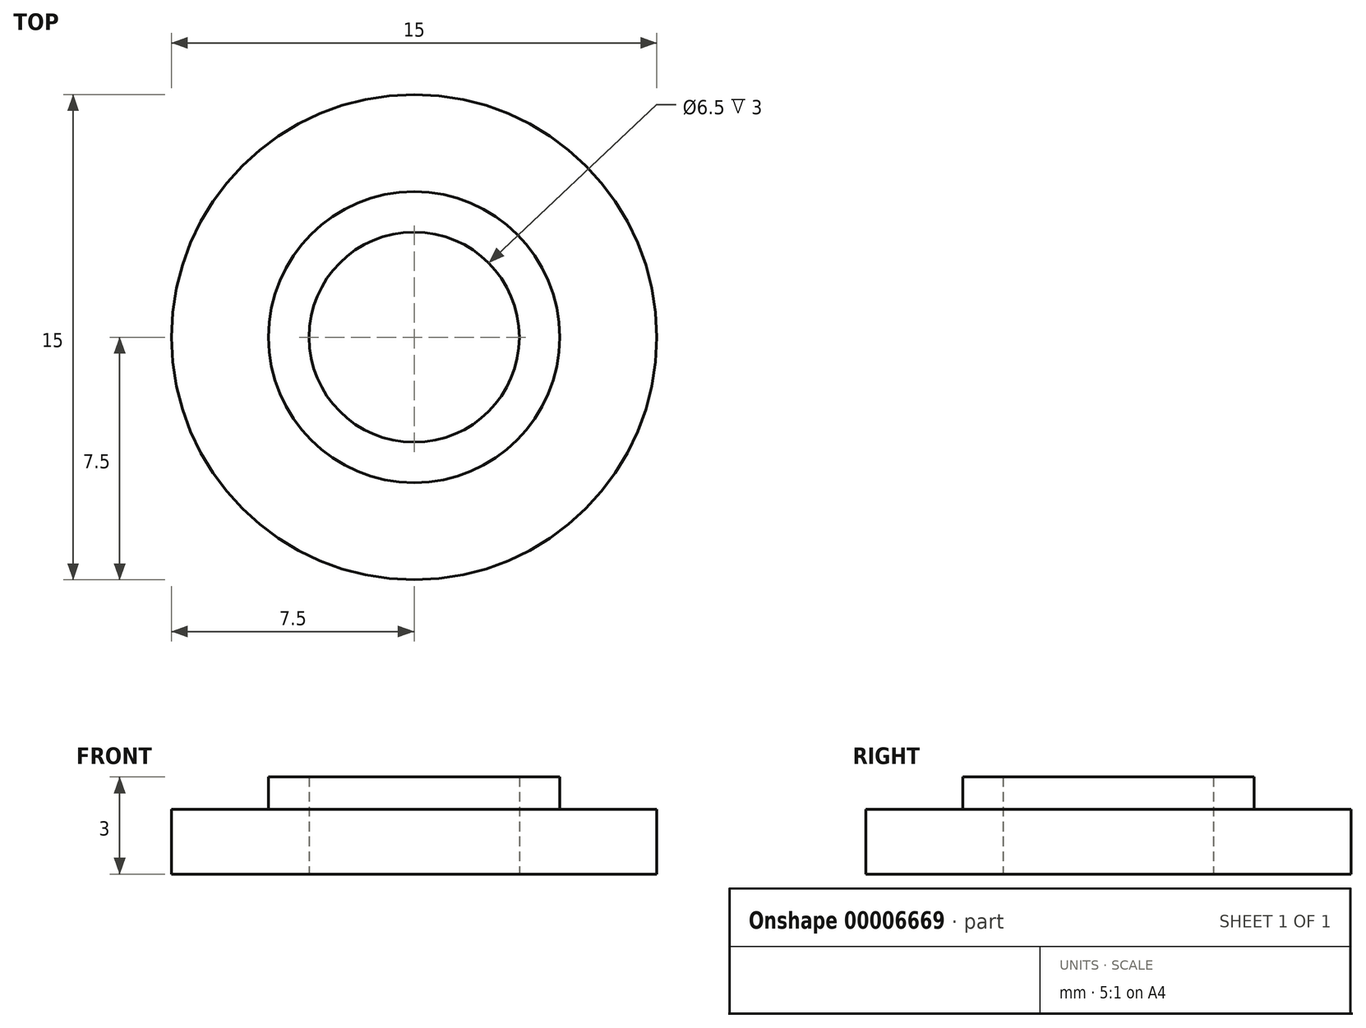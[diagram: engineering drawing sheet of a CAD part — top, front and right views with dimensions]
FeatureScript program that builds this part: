
annotation { "Feature Type Name" : "Feature", "Feature Type Description" : "" }
export const myFeature = defineFeature(function(context is Context, id is Id, definition is map)
    precondition{}
    {
        {
            var Q0;
            Q0=qCreatedBy(makeId("Top.planeOp"),FACE);
            var sketch = newSketch(context, id + "F0", { "sketchPlane" : qUnion([Q0])});
            skCircle(sketch, "E0", {"center": v(0, 0) * mm, "radius": 7.5 * mm});
            skCircle(sketch, "E1", {"center": v(0, 0) * mm, "radius": 3.25 * mm});
            skSolve(sketch);
        }
        {
            var Q0;
            Q0 = qSketchRegion(id + "F0", true);
            extrude(context, id + "F1", {"entities" : qUnion([Q0]), "depth" : 2 * mm});
        }
        {
            var Q0;
            Q0=makeQuery(id+"F1.opExtrude","CAP_FACE",FACE,{"disambiguationData":[OSD([sQuery(id+"F0.wireOp",EDGE,"E0"),sQuery(id+"F0.wireOp",EDGE,"E1")])],"isStart":false});
            var sketch = newSketch(context, id + "F2", { "sketchPlane" : qUnion([Q0])});
            skCircle(sketch, "E2", {"center": v(0, 0) * mm, "radius": 4.5 * mm});
            skCircle(sketch, "E3", {"center": v(0, 0) * mm, "radius": 3.25 * mm});
            skSolve(sketch);
        }
        {
            var Q0;
            Q0 = qSketchRegion(id + "F2", true);
            extrude(context, id + "F3", {"entities" : qUnion([Q0]), "operationType" : NewBodyOperationType.ADD, "depth" : 1 * mm});
        }
    });
